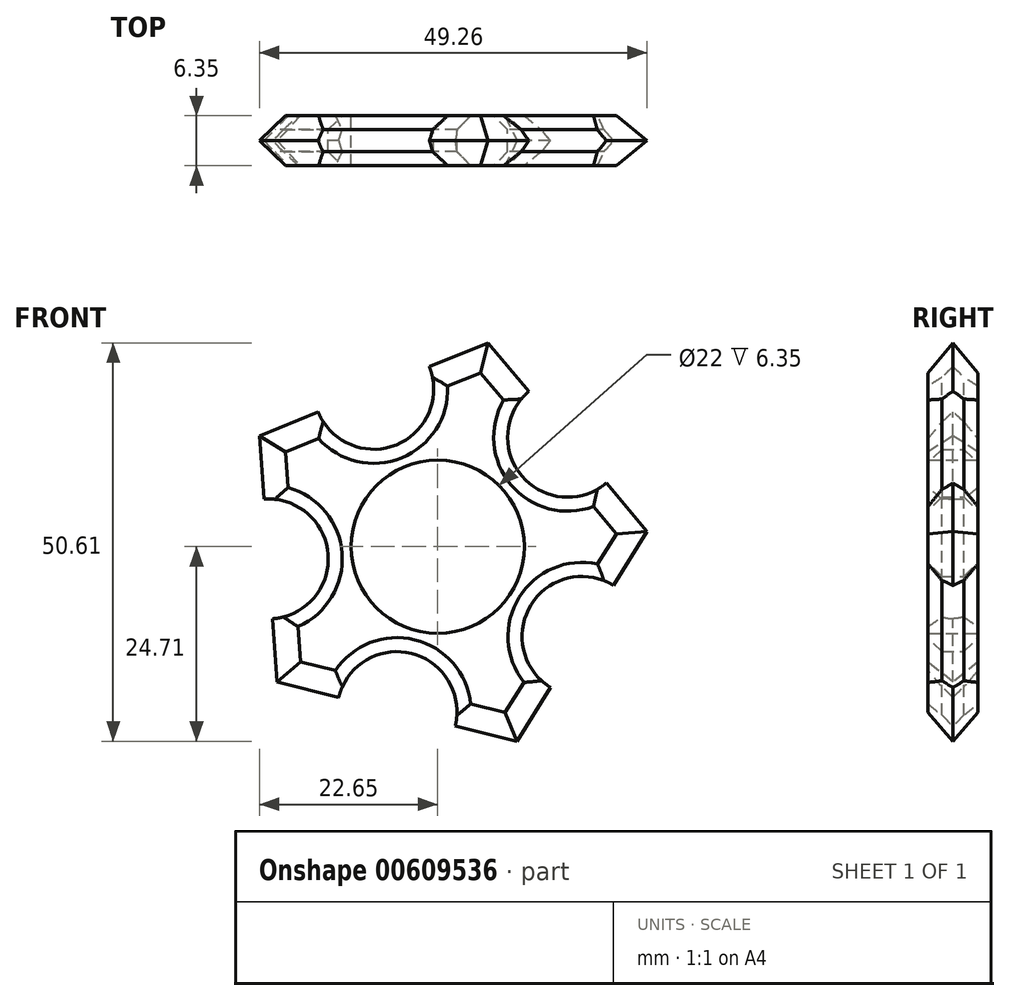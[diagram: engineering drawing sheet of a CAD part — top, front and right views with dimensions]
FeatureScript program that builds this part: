
annotation { "Feature Type Name" : "Feature", "Feature Type Description" : "" }
export const myFeature = defineFeature(function(context is Context, id is Id, definition is map)
    precondition{}
    {
        {
            var Q0;
            Q0=qCreatedBy(makeId("Front.planeOp"),FACE);
            var sketch = newSketch(context, id + "F0", { "sketchPlane" : qUnion([Q0])});
            skCircle(sketch, "E0.cCircle", {"center": v(0, 0) * mm, "radius": 21.58 * mm, "construction": true});
            skLineSegment(sketch, "E0.0", {"start": v(6.4, 25.9) * mm, "end": v(26.6, 1.92) * mm});
            skLineSegment(sketch, "E0.1", {"start": v(26.6, 1.92) * mm, "end": v(10.05, -24.71) * mm});
            skLineSegment(sketch, "E0.2", {"start": v(10.05, -24.71) * mm, "end": v(-20.4, -17.2) * mm});
            skLineSegment(sketch, "E0.3", {"start": v(-20.4, -17.2) * mm, "end": v(-22.65, 14.09) * mm});
            skLineSegment(sketch, "E0.4", {"start": v(-22.65, 14.09) * mm, "end": v(6.4, 25.9) * mm});
            skPoint(sketch, "E0.0.midPoint", {"position": v(16.5, 13.9) * mm});
            skCircle(sketch, "E1", {"center": v(0, 0) * mm, "radius": 11 * mm});
            skCircle(sketch, "E2", {"center": v(16.5, 13.9) * mm, "radius": 7.62 * mm});
            skCircle(sketch, "E3", {"center": v(18.33, -11.4) * mm, "radius": 7.62 * mm});
            skCircle(sketch, "E4", {"center": v(-5.17, -20.95) * mm, "radius": 7.62 * mm});
            skCircle(sketch, "E5", {"center": v(-21.53, -1.55) * mm, "radius": 7.62 * mm});
            skCircle(sketch, "E6", {"center": v(-8.13, 20) * mm, "radius": 7.62 * mm});
            skSolve(sketch);
        }
        {
            var Q0;
            Q0=makeQuery(id+"F0.imprint","IMPRINT",FACE,{"disambiguationData":[TD([[makeQuery(id+"F0.imprint","IMPRINT",EDGE,{"derivedFrom":sQuery(id+"F0.wireOp",EDGE,"E1")}),-1.0]])]});
            extrude(context, id + "F1", {"entities" : qUnion([Q0]), "depth" : 6.35 * mm, "offsetDistance" : 25.4 * mm});
        }
        {
            var Q0;
            {var subQ0=sQuery(id+"F0.wireOp",EDGE,"E0.1");Q0=makeQuery(id+"F1.opExtrude","CAP_EDGE",EDGE,{"disambiguationData":[OSD([subQ0]),TDD([makeQuery(id+"F0.imprint","IMPRINT",EDGE,{"disambiguationData":[TD([[makeQuery(id+"F0.imprint","INTERSECT",VERTEX,{"derivedFrom":[sQuery(id+"F0.wireOp",EDGE,"E0.0"),subQ0]}),-1.0]])],"derivedFrom":subQ0})])],"isStart":false});}
            var Q1;
            {var subQ0=sQuery(id+"F0.wireOp",EDGE,"E0.0");Q1=makeQuery(id+"F1.opExtrude","CAP_EDGE",EDGE,{"disambiguationData":[OSD([subQ0]),TDD([makeQuery(id+"F0.imprint","IMPRINT",EDGE,{"disambiguationData":[TD([[makeQuery(id+"F0.imprint","INTERSECT",VERTEX,{"derivedFrom":[subQ0,sQuery(id+"F0.wireOp",EDGE,"E0.1")]}),1.0]])],"derivedFrom":subQ0})])],"isStart":false});}
            var Q2;
            {var subQ0=sQuery(id+"F0.wireOp",EDGE,"E0.0");Q2=makeQuery(id+"F1.opExtrude","CAP_EDGE",EDGE,{"disambiguationData":[OSD([subQ0]),TDD([makeQuery(id+"F0.imprint","IMPRINT",EDGE,{"disambiguationData":[TD([[makeQuery(id+"F0.imprint","INTERSECT",VERTEX,{"derivedFrom":[subQ0,sQuery(id+"F0.wireOp",EDGE,"E0.4")]}),-1.0]])],"derivedFrom":subQ0})])],"isStart":false});}
            var Q3;
            {var subQ0=sQuery(id+"F0.wireOp",EDGE,"E0.4");Q3=makeQuery(id+"F1.opExtrude","CAP_EDGE",EDGE,{"disambiguationData":[OSD([subQ0]),TDD([makeQuery(id+"F0.imprint","IMPRINT",EDGE,{"disambiguationData":[TD([[makeQuery(id+"F0.imprint","INTERSECT",VERTEX,{"derivedFrom":[sQuery(id+"F0.wireOp",EDGE,"E0.0"),subQ0]}),1.0]])],"derivedFrom":subQ0})])],"isStart":false});}
            var Q4;
            {var subQ0=sQuery(id+"F0.wireOp",EDGE,"E0.4");Q4=makeQuery(id+"F1.opExtrude","CAP_EDGE",EDGE,{"disambiguationData":[OSD([subQ0]),TDD([makeQuery(id+"F0.imprint","IMPRINT",EDGE,{"disambiguationData":[TD([[makeQuery(id+"F0.imprint","INTERSECT",VERTEX,{"derivedFrom":[sQuery(id+"F0.wireOp",EDGE,"E0.3"),subQ0]}),-1.0]])],"derivedFrom":subQ0})])],"isStart":false});}
            var Q5;
            {var subQ0=sQuery(id+"F0.wireOp",EDGE,"E0.3");Q5=makeQuery(id+"F1.opExtrude","CAP_EDGE",EDGE,{"disambiguationData":[OSD([subQ0]),TDD([makeQuery(id+"F0.imprint","IMPRINT",EDGE,{"disambiguationData":[TD([[makeQuery(id+"F0.imprint","INTERSECT",VERTEX,{"derivedFrom":[subQ0,sQuery(id+"F0.wireOp",EDGE,"E0.4")]}),1.0]])],"derivedFrom":subQ0})])],"isStart":false});}
            var Q6;
            {var subQ0=sQuery(id+"F0.wireOp",EDGE,"E0.3");Q6=makeQuery(id+"F1.opExtrude","CAP_EDGE",EDGE,{"disambiguationData":[OSD([subQ0]),TDD([makeQuery(id+"F0.imprint","IMPRINT",EDGE,{"disambiguationData":[TD([[makeQuery(id+"F0.imprint","INTERSECT",VERTEX,{"derivedFrom":[sQuery(id+"F0.wireOp",EDGE,"E0.2"),subQ0]}),-1.0]])],"derivedFrom":subQ0})])],"isStart":false});}
            var Q7;
            {var subQ0=sQuery(id+"F0.wireOp",EDGE,"E0.2");Q7=makeQuery(id+"F1.opExtrude","CAP_EDGE",EDGE,{"disambiguationData":[OSD([subQ0]),TDD([makeQuery(id+"F0.imprint","IMPRINT",EDGE,{"disambiguationData":[TD([[makeQuery(id+"F0.imprint","INTERSECT",VERTEX,{"derivedFrom":[subQ0,sQuery(id+"F0.wireOp",EDGE,"E0.3")]}),1.0]])],"derivedFrom":subQ0})])],"isStart":false});}
            var Q8;
            {var subQ0=sQuery(id+"F0.wireOp",EDGE,"E0.0");Q8=makeQuery(id+"F1.opExtrude","CAP_EDGE",EDGE,{"disambiguationData":[OSD([subQ0]),TDD([makeQuery(id+"F0.imprint","IMPRINT",EDGE,{"disambiguationData":[TD([[makeQuery(id+"F0.imprint","INTERSECT",VERTEX,{"derivedFrom":[subQ0,sQuery(id+"F0.wireOp",EDGE,"E0.1")]}),1.0]])],"derivedFrom":subQ0})])],"isStart":true});}
            var Q9;
            {var subQ0=sQuery(id+"F0.wireOp",EDGE,"E0.1");Q9=makeQuery(id+"F1.opExtrude","CAP_EDGE",EDGE,{"disambiguationData":[OSD([subQ0]),TDD([makeQuery(id+"F0.imprint","IMPRINT",EDGE,{"disambiguationData":[TD([[makeQuery(id+"F0.imprint","INTERSECT",VERTEX,{"derivedFrom":[sQuery(id+"F0.wireOp",EDGE,"E0.0"),subQ0]}),-1.0]])],"derivedFrom":subQ0})])],"isStart":true});}
            var Q10;
            {var subQ0=sQuery(id+"F0.wireOp",EDGE,"E0.0");Q10=makeQuery(id+"F1.opExtrude","CAP_EDGE",EDGE,{"disambiguationData":[OSD([subQ0]),TDD([makeQuery(id+"F0.imprint","IMPRINT",EDGE,{"disambiguationData":[TD([[makeQuery(id+"F0.imprint","INTERSECT",VERTEX,{"derivedFrom":[subQ0,sQuery(id+"F0.wireOp",EDGE,"E0.4")]}),-1.0]])],"derivedFrom":subQ0})])],"isStart":true});}
            var Q11;
            {var subQ0=sQuery(id+"F0.wireOp",EDGE,"E0.4");Q11=makeQuery(id+"F1.opExtrude","CAP_EDGE",EDGE,{"disambiguationData":[OSD([subQ0]),TDD([makeQuery(id+"F0.imprint","IMPRINT",EDGE,{"disambiguationData":[TD([[makeQuery(id+"F0.imprint","INTERSECT",VERTEX,{"derivedFrom":[sQuery(id+"F0.wireOp",EDGE,"E0.0"),subQ0]}),1.0]])],"derivedFrom":subQ0})])],"isStart":true});}
            var Q12;
            {var subQ0=sQuery(id+"F0.wireOp",EDGE,"E0.4");Q12=makeQuery(id+"F1.opExtrude","CAP_EDGE",EDGE,{"disambiguationData":[OSD([subQ0]),TDD([makeQuery(id+"F0.imprint","IMPRINT",EDGE,{"disambiguationData":[TD([[makeQuery(id+"F0.imprint","INTERSECT",VERTEX,{"derivedFrom":[sQuery(id+"F0.wireOp",EDGE,"E0.3"),subQ0]}),-1.0]])],"derivedFrom":subQ0})])],"isStart":true});}
            var Q13;
            {var subQ0=sQuery(id+"F0.wireOp",EDGE,"E0.3");Q13=makeQuery(id+"F1.opExtrude","CAP_EDGE",EDGE,{"disambiguationData":[OSD([subQ0]),TDD([makeQuery(id+"F0.imprint","IMPRINT",EDGE,{"disambiguationData":[TD([[makeQuery(id+"F0.imprint","INTERSECT",VERTEX,{"derivedFrom":[subQ0,sQuery(id+"F0.wireOp",EDGE,"E0.4")]}),1.0]])],"derivedFrom":subQ0})])],"isStart":true});}
            var Q14;
            {var subQ0=sQuery(id+"F0.wireOp",EDGE,"E0.3");Q14=makeQuery(id+"F1.opExtrude","CAP_EDGE",EDGE,{"disambiguationData":[OSD([subQ0]),TDD([makeQuery(id+"F0.imprint","IMPRINT",EDGE,{"disambiguationData":[TD([[makeQuery(id+"F0.imprint","INTERSECT",VERTEX,{"derivedFrom":[sQuery(id+"F0.wireOp",EDGE,"E0.2"),subQ0]}),-1.0]])],"derivedFrom":subQ0})])],"isStart":true});}
            var Q15;
            {var subQ0=sQuery(id+"F0.wireOp",EDGE,"E0.2");Q15=makeQuery(id+"F1.opExtrude","CAP_EDGE",EDGE,{"disambiguationData":[OSD([subQ0]),TDD([makeQuery(id+"F0.imprint","IMPRINT",EDGE,{"disambiguationData":[TD([[makeQuery(id+"F0.imprint","INTERSECT",VERTEX,{"derivedFrom":[subQ0,sQuery(id+"F0.wireOp",EDGE,"E0.3")]}),1.0]])],"derivedFrom":subQ0})])],"isStart":true});}
            var Q16;
            {var subQ0=sQuery(id+"F0.wireOp",EDGE,"E0.2");Q16=makeQuery(id+"F1.opExtrude","CAP_EDGE",EDGE,{"disambiguationData":[OSD([subQ0]),TDD([makeQuery(id+"F0.imprint","IMPRINT",EDGE,{"disambiguationData":[TD([[makeQuery(id+"F0.imprint","INTERSECT",VERTEX,{"derivedFrom":[sQuery(id+"F0.wireOp",EDGE,"E0.1"),subQ0]}),-1.0]])],"derivedFrom":subQ0})])],"isStart":true});}
            var Q17;
            {var subQ0=sQuery(id+"F0.wireOp",EDGE,"E0.1");Q17=makeQuery(id+"F1.opExtrude","CAP_EDGE",EDGE,{"disambiguationData":[OSD([subQ0]),TDD([makeQuery(id+"F0.imprint","IMPRINT",EDGE,{"disambiguationData":[TD([[makeQuery(id+"F0.imprint","INTERSECT",VERTEX,{"derivedFrom":[subQ0,sQuery(id+"F0.wireOp",EDGE,"E0.2")]}),1.0]])],"derivedFrom":subQ0})])],"isStart":true});}
            var Q18;
            {var subQ0=sQuery(id+"F0.wireOp",EDGE,"E0.1");Q18=makeQuery(id+"F1.opExtrude","CAP_EDGE",EDGE,{"disambiguationData":[OSD([subQ0]),TDD([makeQuery(id+"F0.imprint","IMPRINT",EDGE,{"disambiguationData":[TD([[makeQuery(id+"F0.imprint","INTERSECT",VERTEX,{"derivedFrom":[subQ0,sQuery(id+"F0.wireOp",EDGE,"E0.2")]}),1.0]])],"derivedFrom":subQ0})])],"isStart":false});}
            var Q19;
            {var subQ0=sQuery(id+"F0.wireOp",EDGE,"E0.2");Q19=makeQuery(id+"F1.opExtrude","CAP_EDGE",EDGE,{"disambiguationData":[OSD([subQ0]),TDD([makeQuery(id+"F0.imprint","IMPRINT",EDGE,{"disambiguationData":[TD([[makeQuery(id+"F0.imprint","INTERSECT",VERTEX,{"derivedFrom":[sQuery(id+"F0.wireOp",EDGE,"E0.1"),subQ0]}),-1.0]])],"derivedFrom":subQ0})])],"isStart":false});}
            chamfer(context, id + "F2", {"entities" : qUnion([Q0, Q1, Q2, Q3, Q4, Q5, Q6, Q7, Q8, Q9, Q10, Q11, Q12, Q13, Q14, Q15, Q16, Q17, Q18, Q19]), "width" : 3.17 * mm, "tangentPropagation" : true});
        }
        {
            var Q0;
            Q0=makeQuery(id+"F1.opExtrude","CAP_EDGE",EDGE,{"disambiguationData":[OSD([sQuery(id+"F0.wireOp",EDGE,"E3")])],"isStart":true});
            var Q1;
            Q1=makeQuery(id+"F1.opExtrude","CAP_EDGE",EDGE,{"disambiguationData":[OSD([sQuery(id+"F0.wireOp",EDGE,"E3")])],"isStart":false});
            var Q2;
            Q2=makeQuery(id+"F1.opExtrude","CAP_EDGE",EDGE,{"disambiguationData":[OSD([sQuery(id+"F0.wireOp",EDGE,"E4")])],"isStart":false});
            var Q3;
            Q3=makeQuery(id+"F1.opExtrude","CAP_EDGE",EDGE,{"disambiguationData":[OSD([sQuery(id+"F0.wireOp",EDGE,"E4")])],"isStart":true});
            var Q4;
            Q4=makeQuery(id+"F1.opExtrude","CAP_EDGE",EDGE,{"disambiguationData":[OSD([sQuery(id+"F0.wireOp",EDGE,"E5")])],"isStart":false});
            var Q5;
            Q5=makeQuery(id+"F1.opExtrude","CAP_EDGE",EDGE,{"disambiguationData":[OSD([sQuery(id+"F0.wireOp",EDGE,"E5")])],"isStart":true});
            var Q6;
            Q6=makeQuery(id+"F1.opExtrude","CAP_EDGE",EDGE,{"disambiguationData":[OSD([sQuery(id+"F0.wireOp",EDGE,"E6")])],"isStart":false});
            var Q7;
            Q7=makeQuery(id+"F1.opExtrude","CAP_EDGE",EDGE,{"disambiguationData":[OSD([sQuery(id+"F0.wireOp",EDGE,"E6")])],"isStart":true});
            var Q8;
            Q8=makeQuery(id+"F1.opExtrude","CAP_EDGE",EDGE,{"disambiguationData":[OSD([sQuery(id+"F0.wireOp",EDGE,"E2")])],"isStart":false});
            var Q9;
            Q9=makeQuery(id+"F1.opExtrude","CAP_EDGE",EDGE,{"disambiguationData":[OSD([sQuery(id+"F0.wireOp",EDGE,"E2")])],"isStart":true});
            chamfer(context, id + "F3", {"entities" : qUnion([Q0, Q1, Q2, Q3, Q4, Q5, Q6, Q7, Q8, Q9]), "width" : 1.78 * mm, "tangentPropagation" : true});
        }
    });
